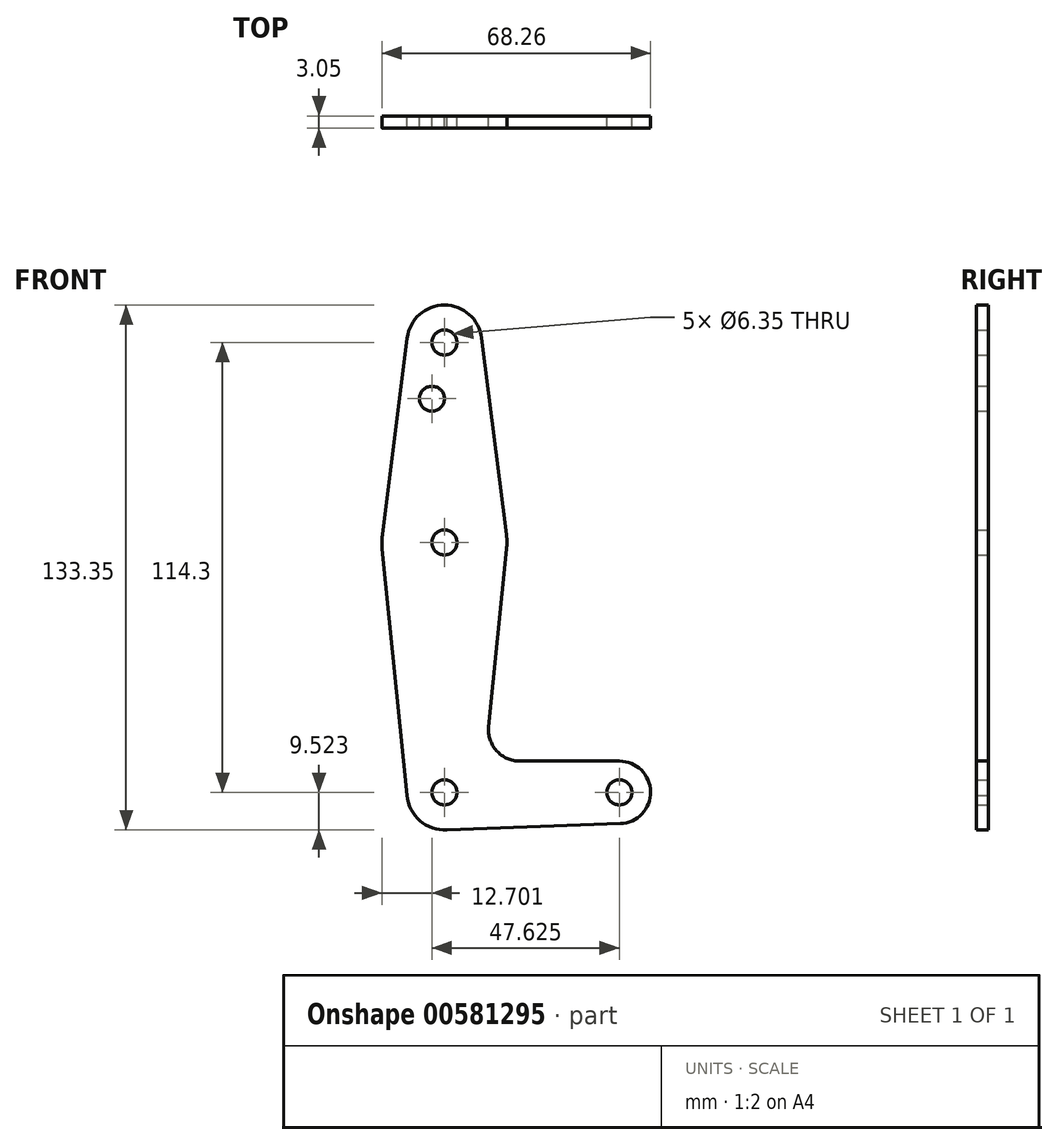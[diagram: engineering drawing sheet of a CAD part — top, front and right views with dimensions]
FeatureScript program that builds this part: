
annotation { "Feature Type Name" : "Feature", "Feature Type Description" : "" }
export const myFeature = defineFeature(function(context is Context, id is Id, definition is map)
    precondition{}
    {
        {
            var Q0;
            Q0=qCreatedBy(makeId("Front.planeOp"),FACE);
            var sketch = newSketch(context, id + "F0", { "sketchPlane" : qUnion([Q0])});
            skCircle(sketch, "E0", {"center": v(-40.37, 56.64) * mm, "radius": 9.53 * mm});
            skLineSegment(sketch, "E1", {"start": v(-40.37, 56.64) * mm, "end": v(-40.37, -57.66) * mm, "construction": true});
            skCircle(sketch, "E2", {"center": v(-40.37, -57.66) * mm, "radius": 9.53 * mm});
            skCircle(sketch, "E3", {"center": v(-40.37, 5.84) * mm, "radius": 15.88 * mm});
            skLineSegment(sketch, "E4", {"start": v(-40.37, -57.66) * mm, "end": v(4.08, -57.66) * mm, "construction": true});
            skCircle(sketch, "E5", {"center": v(4.08, -57.66) * mm, "radius": 7.94 * mm});
            skLineSegment(sketch, "E6", {"start": v(4.36, -65.6) * mm, "end": v(-40.37, -67.18) * mm});
            skLineSegment(sketch, "E7", {"start": v(-21.22, -49.72) * mm, "end": v(4.08, -49.72) * mm});
            skLineSegment(sketch, "E8", {"start": v(-49.82, 57.83) * mm, "end": v(-56.12, 7.83) * mm});
            skLineSegment(sketch, "E9", {"start": v(-30.92, 57.83) * mm, "end": v(-24.62, 7.83) * mm});
            skLineSegment(sketch, "E10", {"start": v(-49.82, -58.85) * mm, "end": v(-56.17, 4.25) * mm});
            skLineSegment(sketch, "E11", {"start": v(-29.13, -40.97) * mm, "end": v(-24.58, 4.25) * mm});
            skCircle(sketch, "E12", {"center": v(-43.55, 42.37) * mm, "radius": 3.18 * mm});
            skCircle(sketch, "E13", {"center": v(-40.37, 56.64) * mm, "radius": 3.18 * mm});
            skCircle(sketch, "E14", {"center": v(-40.37, 5.84) * mm, "radius": 3.18 * mm});
            skCircle(sketch, "E15", {"center": v(-40.37, -57.66) * mm, "radius": 3.18 * mm});
            skCircle(sketch, "E16", {"center": v(4.08, -57.66) * mm, "radius": 3.18 * mm});
            skArc(sketch, "E17.filletArc", {"start": v(-29.13, -40.97) * mm, "mid": v(-27.11, -47.1) * mm, "end": v(-21.22, -49.72) * mm});
            skCircle(sketch, "E18", {"center": v(-40.37, -57.66) * mm, "radius": 1.38 * mm});
            skSolve(sketch);
        }
        {
            var Q0;
            Q0 = qSketchRegion(id + "F0", true);
            extrude(context, id + "F1", {"entities" : qUnion([Q0]), "depth" : 3.05 * mm, "offsetDistance" : 25.4 * mm});
        }
    });
